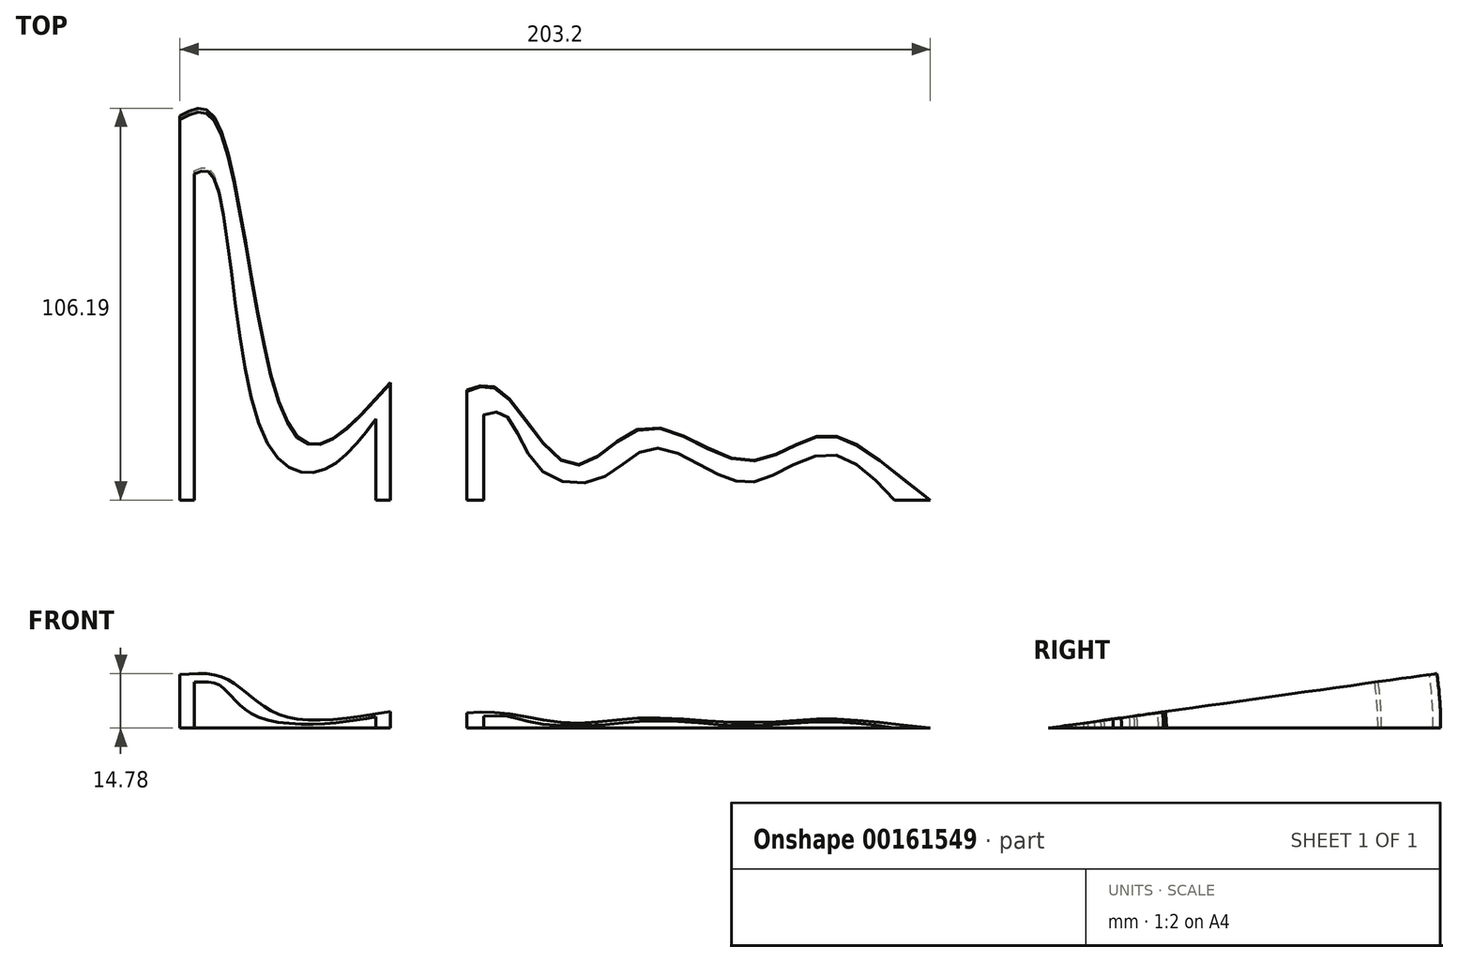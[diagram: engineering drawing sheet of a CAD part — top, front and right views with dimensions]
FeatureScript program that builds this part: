
annotation { "Feature Type Name" : "Feature", "Feature Type Description" : "" }
export const myFeature = defineFeature(function(context is Context, id is Id, definition is map)
    precondition{}
    {
        {
            var Q0;
            Q0=qCreatedBy(makeId("Top.planeOp"),FACE);
            var sketch = newSketch(context, id + "F0", { "sketchPlane" : qUnion([Q0])});
            skLineSegment(sketch, "E0", {"start": v(-106.13, 0) * mm, "end": v(-106.13, 104.14) * mm});
            skFitSpline(sketch, "E1", {"points": [v(-106.13, 104.14) * mm, v(-97.09, 104.14) * mm, v(-74.2, 17) * mm, v(-49.2, 31.9) * mm], "startDerivative": vector(56.51, 31.36) * mm, "endDerivative": vector(91.2, 105.2) * mm});
            skLineSegment(sketch, "E2", {"start": v(-49.2, 31.9) * mm, "end": v(-49.2, 0) * mm});
            skLineSegment(sketch, "E3", {"start": v(-49.2, 0) * mm, "end": v(-106.13, 0) * mm});
            skLineSegment(sketch, "E4", {"start": v(-28.45, 0) * mm, "end": v(-28.45, 29.78) * mm});
            skFitSpline(sketch, "E5", {"points": [v(-28.45, 29.78) * mm, v(-19.41, 29.78) * mm, v(0, 9.56) * mm, v(19.96, 19.67) * mm, v(47.1, 10.62) * mm, v(68.37, 17.54) * mm, v(97.07, 0) * mm], "startDerivative": vector(85.06, 34.2) * mm, "endDerivative": vector(178.4, -130.29) * mm});
            skLineSegment(sketch, "E6", {"start": v(-28.45, 0) * mm, "end": v(97.07, 0) * mm});
            skSolve(sketch);
        }
        {
            var Q0;
            Q0 = qSketchRegion(id + "F0", true);
            var Q1;
            Q1=sQuery(id+"F0.wireOp",EDGE,"E6");
            revolve(context, id + "F1", {"entities" : qUnion([Q0]), "axis" : qUnion([Q1]), "revolveType" : RevolveType.ONE_DIRECTION, "angle" : 8 * degree});
        }
        {
            var Q0;
            Q0=qCreatedBy(makeId("Top.planeOp"),FACE);
            var sketch = newSketch(context, id + "F2", { "sketchPlane" : qUnion([Q0])});
            skLineSegment(sketch, "E7", {"start": v(-102.21, 0) * mm, "end": v(-102.21, 89.19) * mm});
            skFitSpline(sketch, "E8", {"points": [v(-102.21, 89.19) * mm, v(-97.63, 89.19) * mm, v(-83.47, 17.53) * mm, v(-68.05, 7.95) * mm, v(-53.05, 22.12) * mm], "startDerivative": vector(44.42, 22.82) * mm, "endDerivative": vector(60.5, 79.48) * mm});
            skLineSegment(sketch, "E9", {"start": v(-53.05, 22.12) * mm, "end": v(-53.05, 0) * mm});
            skLineSegment(sketch, "E10", {"start": v(-53.05, 0) * mm, "end": v(-102.21, 0) * mm});
            skLineSegment(sketch, "E11", {"start": v(-23.9, 0) * mm, "end": v(-23.9, 23.37) * mm});
            skFitSpline(sketch, "E12", {"points": [v(-23.9, 23.37) * mm, v(-18.06, 23.37) * mm, v(-8.9, 8.79) * mm, v(7.77, 5.87) * mm, v(21.52, 14.2) * mm, v(38.6, 7.54) * mm, v(51.1, 5.45) * mm, v(69.42, 12.54) * mm, v(87.34, 0) * mm], "startDerivative": vector(81.25, 25.41) * mm, "endDerivative": vector(116.5, -126.5) * mm});
            skLineSegment(sketch, "E13", {"start": v(-23.9, 0) * mm, "end": v(87.34, 0) * mm});
            skSolve(sketch);
        }
        {
            var Q0;
            Q0 = qSketchRegion(id + "F2", true);
            var Q1;
            Q1=sQuery(id+"F2.wireOp",EDGE,"E13");
            revolve(context, id + "F3", {"operationType" : NewBodyOperationType.REMOVE, "entities" : qUnion([Q0]), "axis" : qUnion([Q1]), "revolveType" : RevolveType.FULL, "oppositeDirection" : true});
        }
    });
